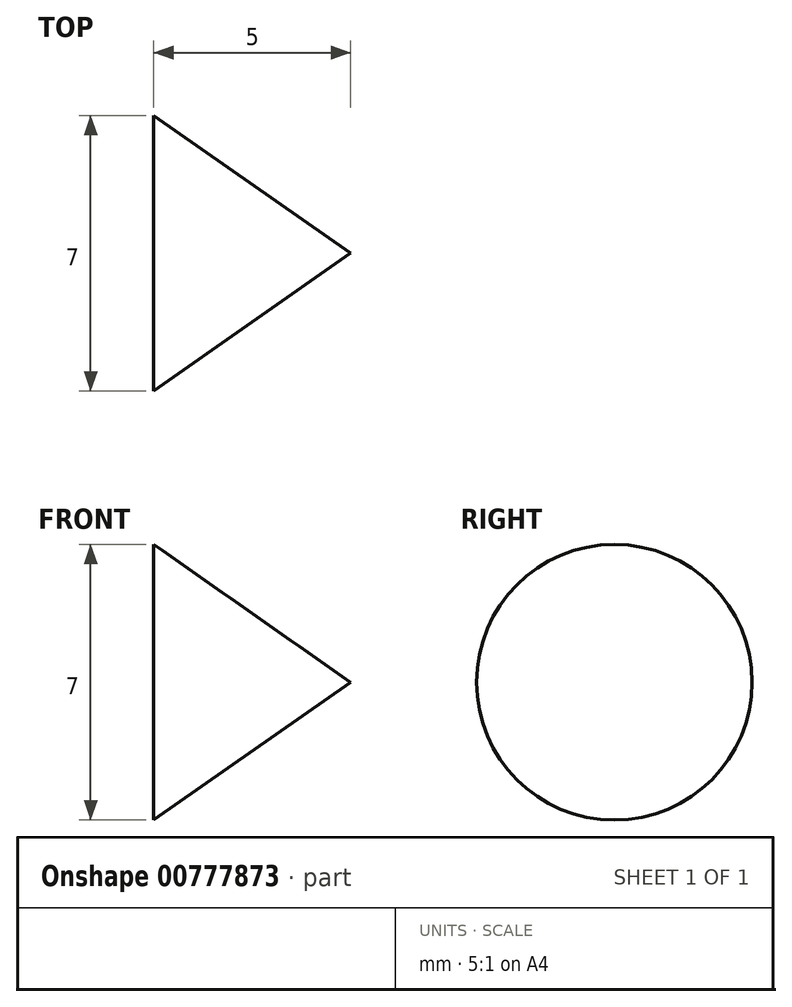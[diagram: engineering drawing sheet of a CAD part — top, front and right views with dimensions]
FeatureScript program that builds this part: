
annotation { "Feature Type Name" : "Feature", "Feature Type Description" : "" }
export const myFeature = defineFeature(function(context is Context, id is Id, definition is map)
    precondition{}
    {
        {
            var Q0;
            Q0=qCreatedBy(makeId("Front.planeOp"),FACE);
            var sketch = newSketch(context, id + "F0", { "sketchPlane" : qUnion([Q0])});
            skLineSegment(sketch, "E0", {"start": v(0, 3.5) * mm, "end": v(0, 0) * mm});
            skLineSegment(sketch, "E1", {"start": v(5, 0) * mm, "end": v(0, 3.5) * mm});
            skLineSegment(sketch, "E2", {"start": v(0, 0) * mm, "end": v(5, 0) * mm});
            skSolve(sketch);
        }
        {
            var Q0;
            Q0=makeQuery(id+"F0.imprint","IMPRINT",FACE,{"disambiguationData":[TD([[makeQuery(id+"F0.imprint","IMPRINT",EDGE,{"derivedFrom":sQuery(id+"F0.wireOp",EDGE,"E0")}),1.0]])]});
            var Q1;
            Q1=sQuery(id+"F0.wireOp",EDGE,"E2");
            revolve(context, id + "F1", {"surfaceOperationType" : NewSurfaceOperationType.NEW, "entities" : qUnion([Q0]), "axis" : qUnion([Q1]), "revolveType" : RevolveType.FULL});
        }
    });
